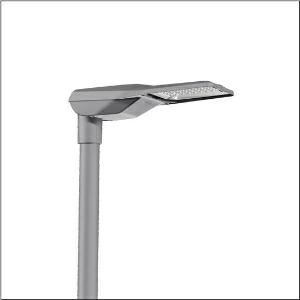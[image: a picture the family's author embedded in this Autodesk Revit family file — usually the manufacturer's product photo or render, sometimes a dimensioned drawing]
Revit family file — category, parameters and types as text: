
# Revit family: streetlight_sl_21_iq_mini___stw1_0a_5xe2e31d08gb_aef3
name_source: partatom
category: Lighting Fixtures
units: mm (PartAtom-declared; Revit-internal decimal feet)

## family parameters
Cut with Voids When Loaded = No
Host = Face
Light Source = No
Part Type = Normal
Room Calculation Point = No
Round Connector Dimension = Use Diameter
Shared = No

## types (1)
- --- (1 x LED, 5680 lm, 37.1 W, 3000K)
    Apparent Load = 37 VA
    CIE Flux Codes = 38 75 98 100 100
    Color Rendering = 70
    Color Temperature = 3000K
    Default Elevation = 1800 mm
    Description = Streetlight SL 21 iQ mini, mast luminaire, primary light control with lens, of PMMA, primary optical cover: cover, of toughened safety glass, transparent, light distribution: STW1.0a, light emission: direct distribution, primary light characteristic: asymmetric, installation type: post-top, side-entry, LED, High Power LED, rated luminous flux: 5.680lm, luminous efficacy: 153lm/W, light colour: 730, colour temperature: 3000K, control: Auto-Match, Temp-Guard, Lumen-Switch, Night-Set, Smart-Wire, Light-Fading, Desk-Remote (wireless, voltage-free reading and setting of iQ features in the workshop via application-optimized NFC function/RFID function), optimised constant luminous flux control (CLO 2.0), presetting dimming linear, mains connection: 220..240V, AC, 50/60Hz, start of lifetime: 37W, end of service life: 39W, reduction: 18W, luminaire housing, of diecast aluminium, powder-coated, Siteco® metallic grey (DB 702S), corrosivity category C5 mid according to DIN EN ISO 12944, please order mast flange separately, inclination adjustable: 0°, 5°, 10°, 15°, sealing non-destructively replaceable, multi-level sealing system, length: 628mm, width: 235mm, height: 110mm, mast flange for spigot size: 42mm (side-entry): 5XC10008XM4, 60/48mm (side-entry/post-top): 5XC10108XM2, 76/60mm (side-entry/post-top): 5XC10108XM1, protection rating (complete): IP66, insulation class (complete): insulation class II (safety insulation), certification: CE, ENEC, ENEC+, VDE, impact resistance: IK09, permissible operating ambient temperature for outdoor applications: -40..+50°C, standard-compliant lighting for roads and squares, packaging unit: 1 piece

Light Distribution: STW1.0a
    Height = 110 mm
    Lamp = 1 x LED
    Lamp Light Flux = 5680 lm
    Lamp Power = 37.1 W
    Lamp count = 1
    Length = 625 mm
    Luminous efficacy = 153 lm/W
    Manufacturer = Siteco
    ModVariant = No
    Model = 5XE2E31D08GB
    Number of Poles = 1
    OnlyDefault = Yes
    Power Factor = 1
    Product Name = Streetlight SL 21 iQ mini | STW1.0a
    Product group = mast luminaire | pylon top
    ProductGroupID = 6100
    Protection Class = Protection class II
    Protection Degree = IP 66
    RLX_Detail_Level = 1
    RLX_Emergency_Light_Flux = 0 lm
    RLX_Emergency_Type = 0
    RLX_Emergency_Type_DB = No
    RlxData = <blob elided: 92281 chars, md5=43df3611>
    Socket = socket
    Standby Power = 0 W
    System Light Flux = 5680 lm
    System Power = 37 W
    Type Comments = factory setting: luminous flux: 100 % | dim-lin: 254 | 385 mA
    Type Image = l_1003519.jpg
    URL = http://relux.com
    VarID = @adj_121095
    Voltage = 0 V
    Weight = 0.00 kg
    Width = 234 mm

## geometry (parser evidence)
native form markers: Blend x4, Sweep x12
no freeform markers — native parametric forms only
